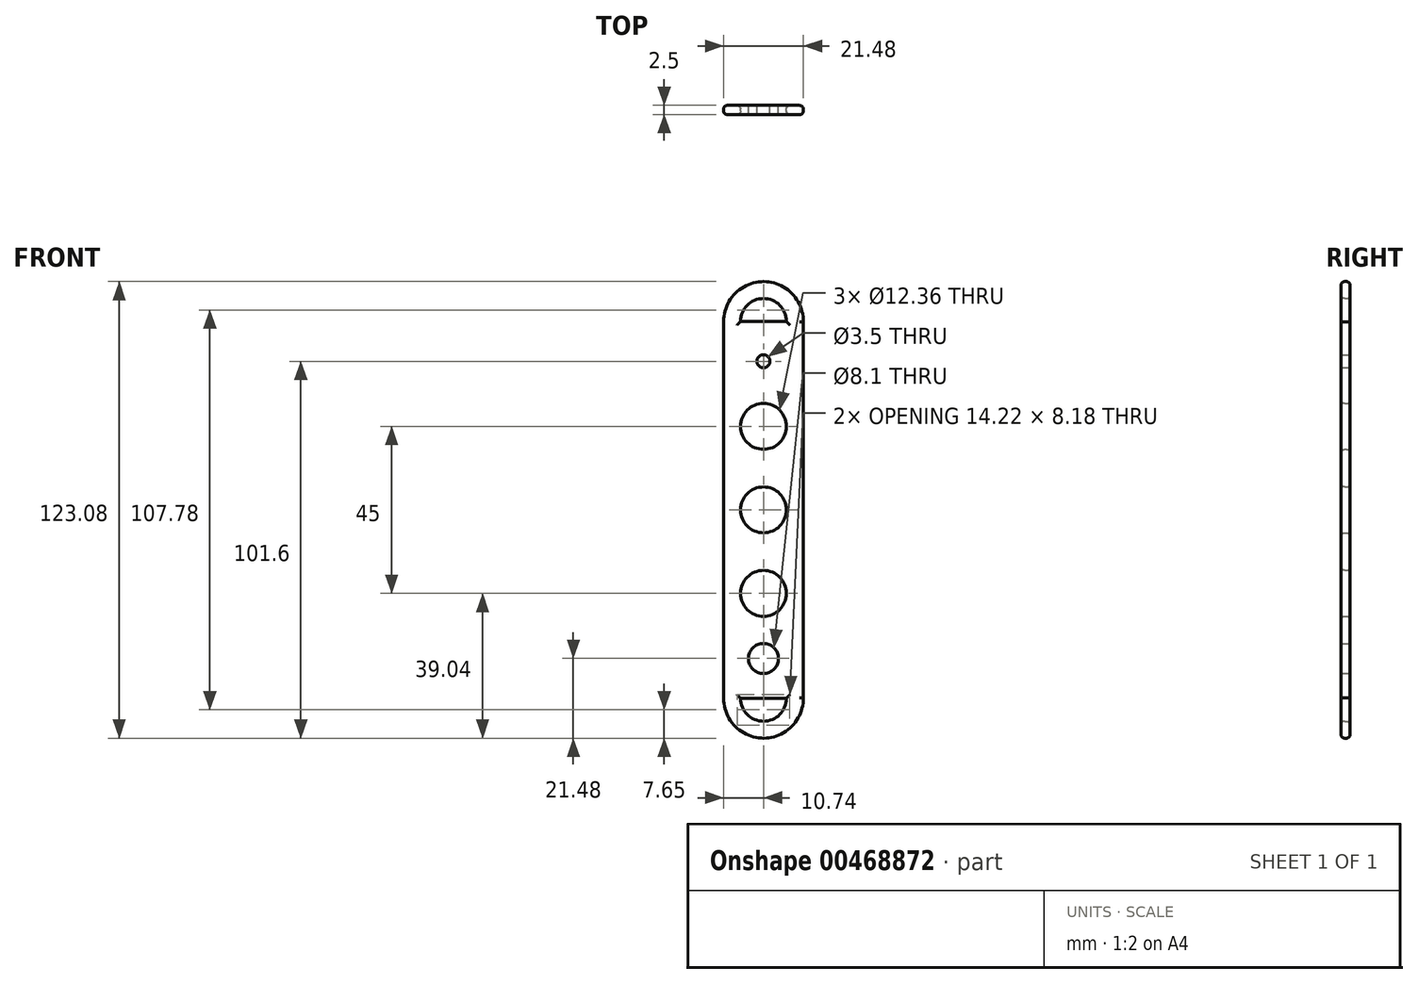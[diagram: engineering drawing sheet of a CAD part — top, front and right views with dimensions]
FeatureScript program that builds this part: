
annotation { "Feature Type Name" : "Feature", "Feature Type Description" : "" }
export const myFeature = defineFeature(function(context is Context, id is Id, definition is map)
    precondition{}
    {
        {
            var Q0;
            Q0=qCreatedBy(makeId("Front.planeOp"),FACE);
            var sketch = newSketch(context, id + "F0", { "sketchPlane" : qUnion([Q0])});
            skPoint(sketch, "E0.middle", {"position": v(0, 0) * mm});
            skLineSegment(sketch, "E1", {"start": v(0, -23.31) * mm, "end": v(0, -31.41) * mm});
            skLineSegment(sketch, "E2", {"start": v(0, 51) * mm, "end": v(0, 54.51) * mm});
            skArc(sketch, "E3", {"start": v(-6.18, -38.1) * mm, "mid": v(0, -44.28) * mm, "end": v(6.18, -38.1) * mm});
            skArc(sketch, "E4", {"start": v(-10.74, -38.1) * mm, "mid": v(0.07, -48.84) * mm, "end": v(10.74, -37.97) * mm});
            skCircle(sketch, "E5", {"center": v(0, -27.36) * mm, "radius": 4.05 * mm});
            skLineSegment(sketch, "E6", {"start": v(6.18, -38.1) * mm, "end": v(-6.18, -38.1) * mm});
            skLineSegment(sketch, "E7", {"start": v(-6.18, -38.1) * mm, "end": v(-6.18, -38.1) * mm});
            skArc(sketch, "E8", {"start": v(6.18, 63.5) * mm, "mid": v(0, 69.68) * mm, "end": v(-6.18, 63.5) * mm});
            skArc(sketch, "E9", {"start": v(10.74, 63.37) * mm, "mid": v(0.07, 74.24) * mm, "end": v(-10.74, 63.5) * mm});
            skCircle(sketch, "E10", {"center": v(0, 52.76) * mm, "radius": 1.75 * mm});
            skLineSegment(sketch, "E11", {"start": v(6.18, 63.5) * mm, "end": v(-6.18, 63.5) * mm});
            skLineSegment(sketch, "E12", {"start": v(-10.74, 63.5) * mm, "end": v(-10.74, -38.1) * mm});
            skLineSegment(sketch, "E13", {"start": v(10.74, -37.97) * mm, "end": v(10.74, 63.63) * mm});
            skLineSegment(sketch, "E14", {"start": v(6.18, 12.7) * mm, "end": v(-6.18, 12.7) * mm, "construction": true});
            skCircle(sketch, "E15", {"center": v(0, 12.7) * mm, "radius": 6.18 * mm});
            skCircle(sketch, "E16.0.1.0", {"center": v(0, 35.2) * mm, "radius": 6.18 * mm});
            skLineSegment(sketch, "E16.direction1", {"start": v(0, 12.7) * mm, "end": v(25, 12.7) * mm, "construction": true});
            skLineSegment(sketch, "E16.direction2", {"start": v(0, 12.7) * mm, "end": v(0, 35.2) * mm, "construction": true});
            skCircle(sketch, "E17.0.1.0", {"center": v(0, -9.8) * mm, "radius": 6.18 * mm});
            skLineSegment(sketch, "E17.direction2", {"start": v(0, 12.7) * mm, "end": v(0, -9.8) * mm, "construction": true});
            skSolve(sketch);
        }
        {
            var Q0;
            Q0 = qSketchRegion(id + "F0", true);
            extrude(context, id + "F1", {"entities" : qUnion([Q0]), "depth" : 2.5 * mm});
        }
        {
            var Q0;
            Q0=makeQuery(id+"F1.opExtrude","CAP_EDGE",EDGE,{"disambiguationData":[OSD([sQuery(id+"F0.wireOp",EDGE,"E8")])],"isStart":false});
            var Q1;
            Q1=makeQuery(id+"F1.opExtrude","CAP_EDGE",EDGE,{"disambiguationData":[OSD([sQuery(id+"F0.wireOp",EDGE,"E8")])],"isStart":true});
            var Q2;
            Q2=makeQuery(id+"F1.opExtrude","CAP_EDGE",EDGE,{"disambiguationData":[OSD([sQuery(id+"F0.wireOp",EDGE,"E11")])],"isStart":false});
            var Q3;
            Q3=makeQuery(id+"F1.opExtrude","CAP_EDGE",EDGE,{"disambiguationData":[OSD([sQuery(id+"F0.wireOp",EDGE,"E11")])],"isStart":true});
            var Q4;
            Q4=makeQuery(id+"F1.opExtrude","CAP_EDGE",EDGE,{"disambiguationData":[OSD([sQuery(id+"F0.wireOp",EDGE,"E9")])],"isStart":false});
            var Q5;
            Q5=makeQuery(id+"F1.opExtrude","CAP_EDGE",EDGE,{"disambiguationData":[OSD([sQuery(id+"F0.wireOp",EDGE,"E9")])],"isStart":true});
            var Q6;
            Q6=makeQuery(id+"F1.opExtrude","CAP_EDGE",EDGE,{"disambiguationData":[OSD([sQuery(id+"F0.wireOp",EDGE,"E16.0.1.0")])],"isStart":false});
            var Q7;
            Q7=makeQuery(id+"F1.opExtrude","CAP_EDGE",EDGE,{"disambiguationData":[OSD([sQuery(id+"F0.wireOp",EDGE,"E16.0.1.0")])],"isStart":true});
            var Q8;
            Q8=makeQuery(id+"F1.opExtrude","CAP_EDGE",EDGE,{"disambiguationData":[OSD([sQuery(id+"F0.wireOp",EDGE,"E15")])],"isStart":false});
            var Q9;
            Q9=makeQuery(id+"F1.opExtrude","CAP_EDGE",EDGE,{"disambiguationData":[OSD([sQuery(id+"F0.wireOp",EDGE,"E15")])],"isStart":true});
            var Q10;
            Q10=makeQuery(id+"F1.opExtrude","CAP_EDGE",EDGE,{"disambiguationData":[OSD([sQuery(id+"F0.wireOp",EDGE,"E17.0.1.0")])],"isStart":false});
            var Q11;
            Q11=makeQuery(id+"F1.opExtrude","CAP_EDGE",EDGE,{"disambiguationData":[OSD([sQuery(id+"F0.wireOp",EDGE,"E17.0.1.0")])],"isStart":true});
            var Q12;
            Q12=makeQuery(id+"F1.opExtrude","CAP_EDGE",EDGE,{"disambiguationData":[OSD([sQuery(id+"F0.wireOp",EDGE,"E6")])],"isStart":false});
            var Q13;
            Q13=makeQuery(id+"F1.opExtrude","CAP_EDGE",EDGE,{"disambiguationData":[OSD([sQuery(id+"F0.wireOp",EDGE,"E6")])],"isStart":true});
            var Q14;
            Q14=makeQuery(id+"F1.opExtrude","CAP_EDGE",EDGE,{"disambiguationData":[OSD([sQuery(id+"F0.wireOp",EDGE,"E3")])],"isStart":true});
            var Q15;
            Q15=makeQuery(id+"F1.opExtrude","CAP_EDGE",EDGE,{"disambiguationData":[OSD([sQuery(id+"F0.wireOp",EDGE,"E3")])],"isStart":false});
            fillet(context, id + "F2", {"entities" : qUnion([Q0, Q1, Q2, Q3, Q4, Q5, Q6, Q7, Q8, Q9, Q10, Q11, Q12, Q13, Q14, Q15]), "radius" : 1 * mm, "tangentPropagation" : true, "allowEdgeOverflow" : false});
        }
    });
